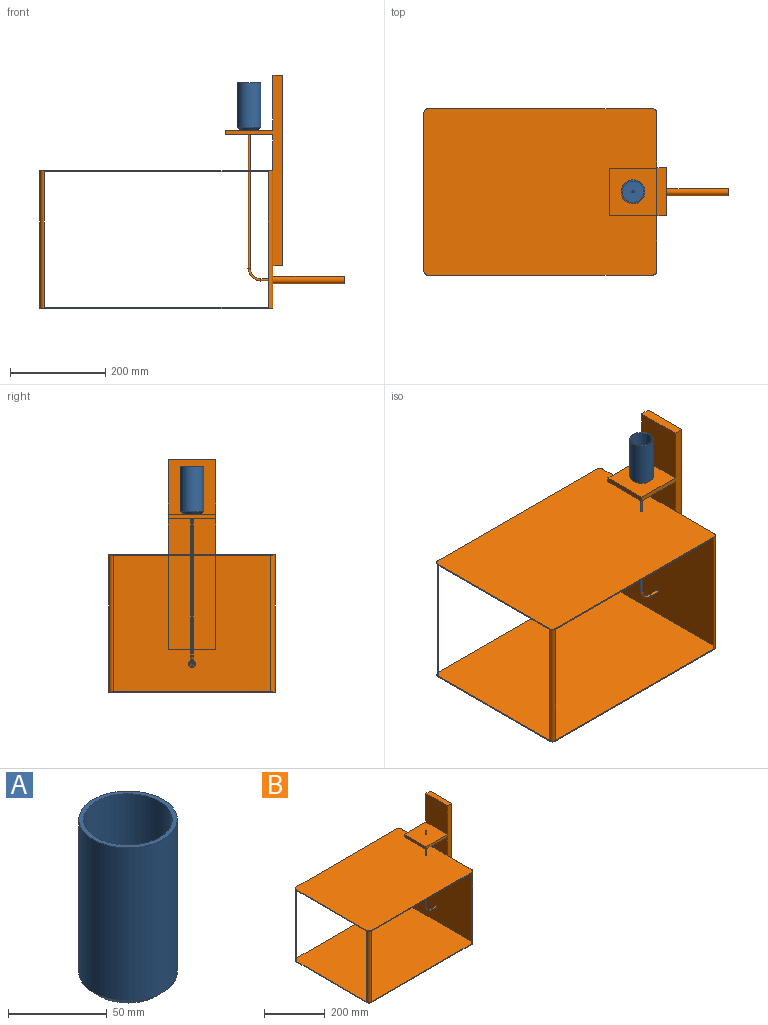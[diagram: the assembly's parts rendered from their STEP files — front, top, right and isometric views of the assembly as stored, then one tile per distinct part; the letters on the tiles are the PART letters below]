
ASSEMBLY  parts=2 mates=1
PART A: 8 faces, bbox 50x50x100 mm
  f0: cylinder r=2.5mm len=5mm, axis (0,0,-1), area 15.7mm2, adj f4,f7
  f1: cylinder r=25mm len=95mm, axis (0,0,-1), area 14922.6mm2, adj f2,f5
  f2: plane 50x50mm, normal (0,0,1), area 373.1mm2, adj f1,f6
  f3: plane 40x40mm, normal (0,0,-1), area 1079.9mm2, adj f4,f5
  f4: cone r=7.5mm half-angle=45deg, axis (0,0,-1), area 222.1mm2, adj f0,f3
  f5: cone r=25mm half-angle=45deg, axis (0,0,1), area 999.6mm2, adj f1,f3
  f6: cylinder r=22.5mm len=94mm, axis (0,0,1), area 13288.9mm2, adj f2,f7
  f7: plane 45x45mm, normal (0,0,1), area 1570.8mm2, adj f0,f6
PART B: 54 faces, bbox 640x350x490 mm
  f0: plane 115x100mm, normal (-1,0,0), area 11500mm2, adj f27,f28,f29,f33
  f1: plane 470x2.5mm, normal (0,1,0), area 1175mm2, adj f9,f11,f13,f26
  f2: plane 470x2.5mm, normal (0,-1,0), area 1175mm2, adj f5,f7,f13,f26
  f3: plane 330x2.5mm, normal (-1,0,0), area 825mm2, adj f5,f11,f13,f26
  f4: plane 330x2.5mm, normal (-1,0,0), area 825mm2, adj f5,f11,f12,f25
  f5: cylinder r=10mm len=290mm, axis (0,0,-1), area 4555.3mm2, adj f2,f3,f4,f6,f12,f13,f15,f16
  f6: plane 470x2.5mm, normal (0,-1,0), area 1175mm2, adj f5,f7,f12,f25
  f7: cylinder r=10mm len=290mm, axis (0,0,-1), area 4555.3mm2, adj f2,f6,f8,f12,f13,f17
  f8: plane 330x290mm, normal (1,0,0), area 75523.3mm2, adj f7,f9,f12,f13,f27,f29,f30,f48
  f9: cylinder r=10mm len=290mm, axis (0,0,-1), area 4555.3mm2, adj f1,f8,f10,f12,f13,f18
  f10: plane 470x2.5mm, normal (0,1,0), area 1175mm2, adj f9,f11,f12,f25
  f11: cylinder r=10mm len=290mm, axis (0,0,-1), area 4555.3mm2, adj f1,f3,f4,f10,f12,f13,f14,f19
  f12: plane 490x350mm, normal (0,0,1), area 171394.5mm2, adj f4,f5,f6,f7,f8,f9,f10,f11
  f13: plane 490x350mm, normal (0,0,-1), area 171414.2mm2, adj f1,f2,f3,f5,f7,f8,f9,f11
  f14: plane 285x2.5mm, normal (0,-1,0), area 712.5mm2, adj f11,f24,f25,f26
  f15: plane 285x2.5mm, normal (0,1,0), area 712.5mm2, adj f5,f20,f25,f26
  f16: plane 285x2.5mm, normal (1,0,0), area 712.5mm2, adj f5,f20,f25,f26
  f17: plane 285x2.5mm, normal (-1,0,0), area 712.5mm2, adj f7,f21,f25,f26
  f18: plane 285x2.5mm, normal (-1,0,0), area 712.5mm2, adj f9,f23,f25,f26
  f19: plane 285x2.5mm, normal (1,0,0), area 712.5mm2, adj f11,f24,f25,f26
  f20: cylinder r=7.5mm len=285mm, axis (0,0,-1), area 3357.6mm2, adj f15,f16,f25,f26
  f21: cylinder r=7.5mm len=285mm, axis (0,0,-1), area 3357.6mm2, adj f17,f22,f25,f26
  f22: plane 330x285mm, normal (-1,0,0), area 94030.4mm2, adj f21,f23,f25,f26,f42
  f23: cylinder r=7.5mm len=285mm, axis (0,0,-1), area 3357.6mm2, adj f18,f22,f25,f26
  f24: cylinder r=7.5mm len=285mm, axis (0,0,-1), area 3357.6mm2, adj f14,f19,f25,f26
  f25: plane 487.5x350mm, normal (0,0,-1), area 170432.1mm2, adj f4,f6,f10,f14,f15,f16,f17,f18
  f26: plane 487.5x350mm, normal (0,0,1), area 170451.7mm2, adj f1,f2,f3,f14,f15,f16,f17,f18
  f27: plane 400x120mm, normal (0,1,0), area 9000mm2, adj f0,f8,f28,f30,f31,f32,f33,f34
  f28: plane 100x20mm, normal (0,0,1), area 2000mm2, adj f0,f27,f29,f31
  f29: plane 400x120mm, normal (0,-1,0), area 9000mm2, adj f0,f8,f28,f30,f31,f32,f33,f34
  f30: plane 100x20mm, normal (0,0,-1), area 2000mm2, adj f8,f27,f29,f31
  f31: plane 400x100mm, normal (1,0,0), area 40000mm2, adj f27,f28,f29,f30
  f32: plane 100x75mm, normal (-1,0,0), area 7500mm2, adj f12,f27,f29,f34
  f33: plane 100x100mm, normal (0,0,1), area 9980.4mm2, adj f0,f27,f29,f35,f40
  f34: plane 100x100mm, normal (0,0,-1), area 9980.4mm2, adj f27,f29,f32,f35,f36
  f35: plane 100x10mm, normal (-1,0,0), area 1000mm2, adj f27,f29,f33,f34
  f36: cylinder r=2.5mm len=75mm, axis (0,0,1), area 1178.1mm2, adj f12,f34
  f37: plane 5x5mm, normal (0,0,1), area 7.1mm2, adj f38,f40
  f38: cylinder r=2mm len=305mm, axis (0,0,1), area 3832.7mm2, adj f37,f39
  f39: torus R=25mm, axis (0,1,0), area 493.5mm2, adj f38,f41
  f40: cylinder r=2.5mm len=15mm, axis (0,0,1), area 235.6mm2, adj f33,f37
  f41: cylinder r=2mm len=22.5mm, axis (-1,0,0), area 282.7mm2, adj f39,f45
  f42: cylinder r=2.5mm len=22.5mm, axis (-1,0,0), area 353.4mm2, adj f22,f43
  f43: torus R=25mm, axis (0,1,0), area 616.9mm2, adj f42,f44
  f44: cylinder r=2.5mm len=202.5mm, axis (0,0,1), area 3180.9mm2, adj f25,f43
  f45: plane 4x4mm, normal (-1,0,0), area 12.6mm2, adj f41
  f46: cylinder r=6mm len=150mm, axis (1,0,0), area 5654.9mm2, adj f47,f53
  f47: plane 15x15mm, normal (1,0,0), area 63.6mm2, adj f46,f48
  f48: cylinder r=7.5mm len=150mm, axis (1,0,0), area 7068.6mm2, adj f8,f47
  f49: plane 4x4mm, normal (1,0,0), area 12.6mm2, adj f50
  f50: cylinder r=2mm len=25mm, axis (-1,0,0), area 314.2mm2, adj f49,f51
  f51: plane 5x5mm, normal (1,0,0), area 7.1mm2, adj f50,f52
  f52: cylinder r=2.5mm len=25mm, axis (-1,0,0), area 392.7mm2, adj f51,f53
  f53: plane 12x12mm, normal (1,0,0), area 93.5mm2, adj f46,f52
PLACE A t=(-37.84,69.53,370.99)mm
PLACE B t=(-232.84,69.53,-4.01)mm
MATE fastened A.f1 <-> B.f36  axis (0,0,-1) through (-37.84,69.53,370.99)mm
